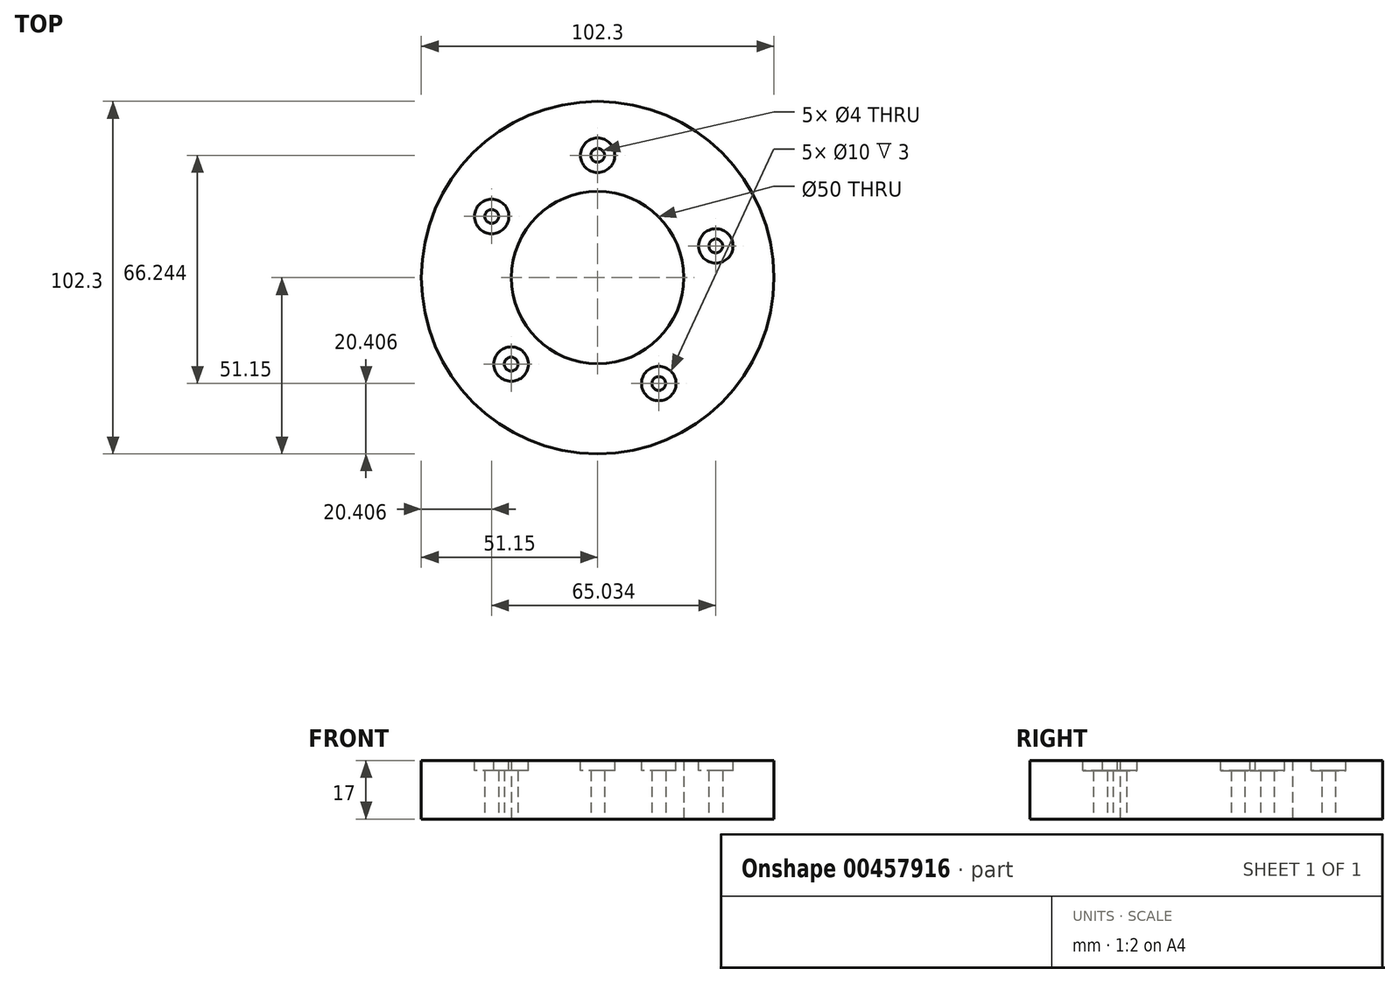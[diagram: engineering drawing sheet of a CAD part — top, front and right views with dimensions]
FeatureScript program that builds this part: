
annotation { "Feature Type Name" : "Feature", "Feature Type Description" : "" }
export const myFeature = defineFeature(function(context is Context, id is Id, definition is map)
    precondition{}
    {
        {
            var Q0;
            Q0=qCreatedBy(makeId("Top.planeOp"),FACE);
            var sketch = newSketch(context, id + "F0", { "sketchPlane" : qUnion([Q0])});
            skCircle(sketch, "E0", {"center": v(0, 0) * mm, "radius": 51.15 * mm});
            skCircle(sketch, "E1", {"center": v(0, 0) * mm, "radius": 25 * mm});
            skCircle(sketch, "E2", {"center": v(0, 35.5) * mm, "radius": 2 * mm});
            skCircle(sketch, "E3.1.0", {"center": v(34.3, 9.19) * mm, "radius": 2 * mm});
            skCircle(sketch, "E3.2.0", {"center": v(17.75, -30.74) * mm, "radius": 2 * mm});
            skCircle(sketch, "E3.3.0", {"center": v(-25.1, -25.1) * mm, "radius": 2 * mm});
            skCircle(sketch, "E3.4.0", {"center": v(-30.74, 17.75) * mm, "radius": 2 * mm});
            skLineSegment(sketch, "E3.anchor1", {"start": v(0, 0) * mm, "end": v(0, 35.5) * mm, "construction": true});
            skLineSegment(sketch, "E3.anchor2", {"start": v(0, 0) * mm, "end": v(-30.74, 17.75) * mm, "construction": true});
            skLineSegment(sketch, "E4", {"start": v(0, 25) * mm, "end": v(0, 28.14) * mm});
            skSolve(sketch);
        }
        {
            var Q0;
            Q0=makeQuery(id+"F0.imprint","IMPRINT",FACE,{"disambiguationData":[TD([[makeQuery(id+"F0.imprint","IMPRINT",EDGE,{"derivedFrom":sQuery(id+"F0.wireOp",EDGE,"E0")}),1.0]])]});
            extrude(context, id + "F1", {"entities" : qUnion([Q0]), "depth" : 17 * mm});
        }
        {
            var Q0;
            Q0=makeQuery(id+"F1.opExtrude","CAP_FACE",FACE,{"disambiguationData":[OSD([sQuery(id+"F0.wireOp",EDGE,"E0"),sQuery(id+"F0.wireOp",EDGE,"E1"),sQuery(id+"F0.wireOp",EDGE,"E2"),sQuery(id+"F0.wireOp",EDGE,"E3.1.0"),sQuery(id+"F0.wireOp",EDGE,"E3.2.0"),sQuery(id+"F0.wireOp",EDGE,"E3.3.0"),sQuery(id+"F0.wireOp",EDGE,"E3.4.0")])],"isStart":false});
            var sketch = newSketch(context, id + "F2", { "sketchPlane" : qUnion([Q0])});
            skCircle(sketch, "E5", {"center": v(0, 35.5) * mm, "radius": 5 * mm});
            skPoint(sketch, "E6.center", {"position": v(0, 0) * mm});
            skLineSegment(sketch, "E6.anchor1", {"start": v(0, 0) * mm, "end": v(0, 35.5) * mm, "construction": true});
            skLineSegment(sketch, "E6.anchor2", {"start": v(0, 0) * mm, "end": v(-33.36, 12.14) * mm, "construction": true});
            skCircle(sketch, "E7", {"center": v(-30.74, 17.75) * mm, "radius": 5 * mm});
            skCircle(sketch, "E8", {"center": v(34.3, 9.19) * mm, "radius": 5 * mm});
            skCircle(sketch, "E9", {"center": v(17.75, -30.74) * mm, "radius": 5 * mm});
            skCircle(sketch, "E10", {"center": v(-25.1, -25.1) * mm, "radius": 5 * mm});
            skSolve(sketch);
        }
        {
            var Q0;
            Q0=makeQuery(id+"F2.imprint","IMPRINT",FACE,{"disambiguationData":[TD([[makeQuery(id+"F2.imprint","IMPRINT",EDGE,{"derivedFrom":sQuery(id+"F2.wireOp",EDGE,"E5")}),1.0]])]});
            var Q1;
            Q1=makeQuery(id+"F2.imprint","IMPRINT",FACE,{"disambiguationData":[TD([[makeQuery(id+"F2.imprint","IMPRINT",EDGE,{"derivedFrom":sQuery(id+"F2.wireOp",EDGE,"E7")}),1.0]])]});
            var Q2;
            Q2=makeQuery(id+"F2.imprint","IMPRINT",FACE,{"disambiguationData":[TD([[makeQuery(id+"F2.imprint","IMPRINT",EDGE,{"derivedFrom":sQuery(id+"F2.wireOp",EDGE,"E10")}),1.0]])]});
            var Q3;
            Q3=makeQuery(id+"F2.imprint","IMPRINT",FACE,{"disambiguationData":[TD([[makeQuery(id+"F2.imprint","IMPRINT",EDGE,{"derivedFrom":sQuery(id+"F2.wireOp",EDGE,"E9")}),1.0]])]});
            var Q4;
            Q4=makeQuery(id+"F2.imprint","IMPRINT",FACE,{"disambiguationData":[TD([[makeQuery(id+"F2.imprint","IMPRINT",EDGE,{"derivedFrom":sQuery(id+"F2.wireOp",EDGE,"E8")}),1.0]])]});
            extrude(context, id + "F3", {"entities" : qUnion([Q0, Q1, Q2, Q3, Q4]), "operationType" : NewBodyOperationType.REMOVE, "oppositeDirection" : true, "depth" : 3 * mm});
        }
    });
